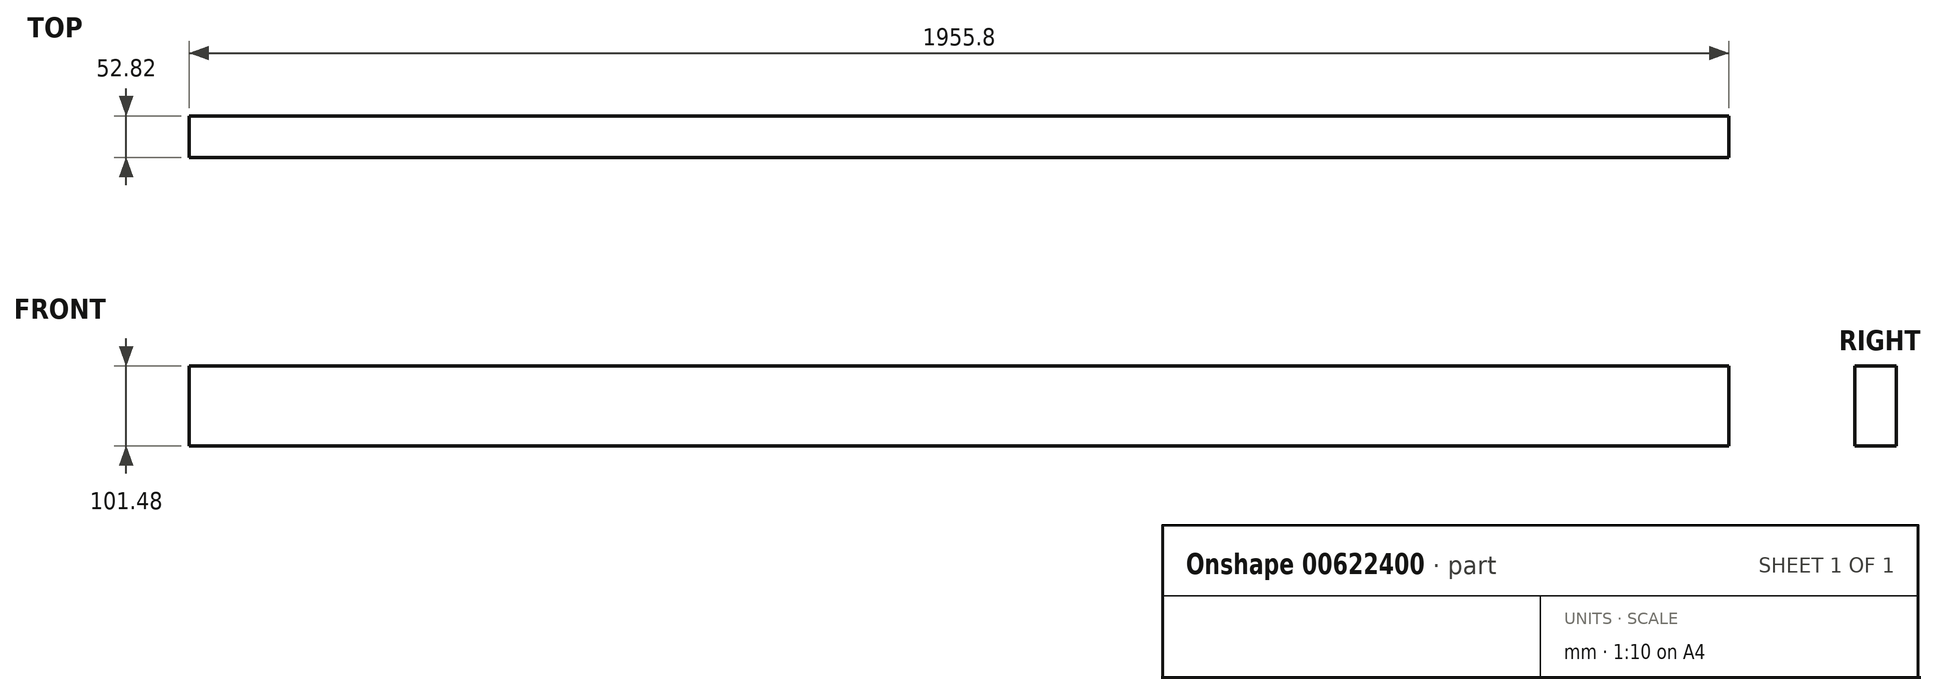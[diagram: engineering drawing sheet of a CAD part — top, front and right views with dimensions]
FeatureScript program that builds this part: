
annotation { "Feature Type Name" : "Feature", "Feature Type Description" : "" }
export const myFeature = defineFeature(function(context is Context, id is Id, definition is map)
    precondition{}
    {
        {
            var Q0;
            Q0=qCreatedBy(makeId("Right.planeOp"),FACE);
            var sketch = newSketch(context, id + "F0", { "sketchPlane" : qUnion([Q0])});
            skLineSegment(sketch, "E0.bottom", {"start": v(-27.87, 38.26) * mm, "end": v(24.95, 38.26) * mm});
            skLineSegment(sketch, "E0.top", {"start": v(-27.87, -63.22) * mm, "end": v(24.95, -63.22) * mm});
            skLineSegment(sketch, "E0.left", {"start": v(-27.87, 38.26) * mm, "end": v(-27.87, -63.22) * mm});
            skLineSegment(sketch, "E0.right", {"start": v(24.95, 38.26) * mm, "end": v(24.95, -63.22) * mm});
            skSolve(sketch);
        }
        {
            var Q0;
            Q0=makeQuery(id+"F0.imprint","IMPRINT",FACE,{"disambiguationData":[TD([[makeQuery(id+"F0.imprint","IMPRINT",EDGE,{"derivedFrom":sQuery(id+"F0.wireOp",EDGE,"E0.bottom")}),-1.0]])]});
            extrude(context, id + "F1", {"entities" : qUnion([Q0]), "depth" : 1955.8 * mm, "offsetDistance" : 25.4 * mm});
        }
    });
